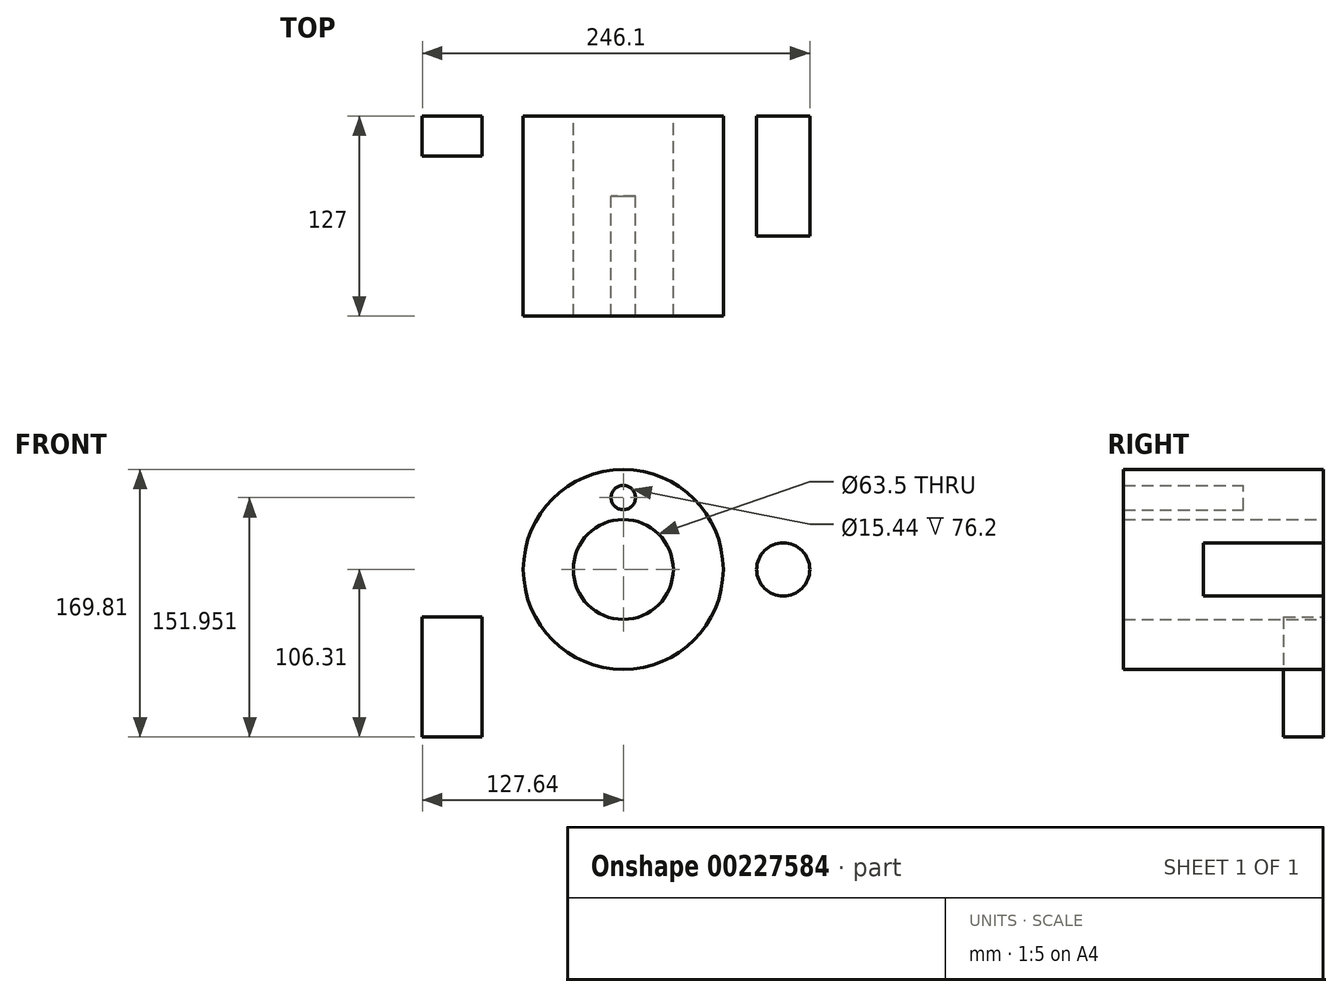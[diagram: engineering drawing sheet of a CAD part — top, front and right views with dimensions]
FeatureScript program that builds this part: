
annotation { "Feature Type Name" : "Feature", "Feature Type Description" : "" }
export const myFeature = defineFeature(function(context is Context, id is Id, definition is map)
    precondition{}
    {
        {
            var Q0;
            Q0=qCreatedBy(makeId("Front.planeOp"),FACE);
            var sketch = newSketch(context, id + "F0", { "sketchPlane" : qUnion([Q0])});
            skCircle(sketch, "E0", {"center": v(0, 0) * mm, "radius": 63.5 * mm});
            skCircle(sketch, "E1", {"center": v(0, 0) * mm, "radius": 31.75 * mm});
            skSolve(sketch);
        }
        {
            var Q0;
            Q0=makeQuery(id+"F0.imprint","IMPRINT",FACE,{"disambiguationData":[TD([[makeQuery(id+"F0.imprint","IMPRINT",EDGE,{"derivedFrom":sQuery(id+"F0.wireOp",EDGE,"E0")}),1.0]])]});
            var Q1;
            Q1 = qSketchRegion(id + "F0", true);
            extrude(context, id + "F1", {"entities" : qUnion([Q0, Q1]), "depth" : 50.8 * mm});
        }
        {
            var Q0;
            Q0=makeQuery(id+"F1.opExtrude","CAP_FACE",FACE,{"disambiguationData":[OSD([sQuery(id+"F0.wireOp",EDGE,"E0"),sQuery(id+"F0.wireOp",EDGE,"E1")])],"isStart":false});
            var sketch = newSketch(context, id + "F2", { "sketchPlane" : qUnion([Q0])});
            skCircle(sketch, "E2", {"center": v(0, 45.64) * mm, "radius": 7.72 * mm});
            skSolve(sketch);
        }
        {
            var Q0;
            Q0 = qSketchRegion(id + "F2", true);
            extrude(context, id + "F3", {"entities" : qUnion([Q0]), "operationType" : NewBodyOperationType.ADD, "oppositeDirection" : true, "depth" : 50.8 * mm});
        }
        {
            var Q0;
            Q0=makeQuery(id+"F2.imprint","IMPRINT",FACE,{"disambiguationData":[TD([[makeQuery(id+"F2.imprint","IMPRINT",EDGE,{"derivedFrom":sQuery(id+"F2.wireOp",EDGE,"E2")}),-1.0]])]});
            var sketch = newSketch(context, id + "F4", { "sketchPlane" : qUnion([Q0])});
            skCircle(sketch, "E3", {"center": v(101.6, 0) * mm, "radius": 16.86 * mm});
            skLineSegment(sketch, "E4", {"start": v(38.29, -51.7) * mm, "end": v(109.34, -14.98) * mm});
            skLineSegment(sketch, "E5", {"start": v(36.14, 52.8) * mm, "end": v(109.34, 14.98) * mm});
            skSolve(sketch);
        }
        {
            var Q0;
            Q0 = qSketchRegion(id + "F4", true);
            extrude(context, id + "F5", {"entities" : qUnion([Q0]), "depth" : 25.4 * mm});
        }
        {
            var Q0;
            Q0=makeQuery(id+"F5.opExtrude","CAP_FACE",FACE,{"disambiguationData":[OSD([sQuery(id+"F4.wireOp",EDGE,"E3")])],"isStart":false});
            extrude(context, id + "F6", {"entities" : qUnion([Q0]), "operationType" : NewBodyOperationType.ADD, "oppositeDirection" : true, "depth" : 76.2 * mm});
        }
        {
            var Q0;
            Q0=makeQuery(id+"F5.opExtrude","CAP_FACE",FACE,{"disambiguationData":[OSD([sQuery(id+"F4.wireOp",EDGE,"E3")])],"isStart":false});
            extrude(context, id + "F7", {"entities" : qUnion([Q0]), "operationType" : NewBodyOperationType.ADD, "oppositeDirection" : true, "depth" : 25.4 * mm});
        }
        {
            var Q0;
            Q0=makeQuery(id+"F2.imprint","IMPRINT",FACE,{"disambiguationData":[TD([[makeQuery(id+"F2.imprint","IMPRINT",EDGE,{"derivedFrom":sQuery(id+"F2.wireOp",EDGE,"E2")}),-1.0]])]});
            extrude(context, id + "F8", {"entities" : qUnion([Q0]), "operationType" : NewBodyOperationType.ADD, "depth" : 76.2 * mm});
        }
        {
            var Q0;
            Q0=qCreatedBy(makeId("Front.planeOp"),FACE);
            var sketch = newSketch(context, id + "F9", { "sketchPlane" : qUnion([Q0])});
            skLineSegment(sketch, "E6.bottom", {"start": v(-127.64, -30.11) * mm, "end": v(-89.54, -30.11) * mm});
            skLineSegment(sketch, "E6.top", {"start": v(-127.64, -106.31) * mm, "end": v(-89.54, -106.31) * mm});
            skLineSegment(sketch, "E6.left", {"start": v(-127.64, -30.11) * mm, "end": v(-127.64, -106.31) * mm});
            skLineSegment(sketch, "E6.right", {"start": v(-89.54, -30.11) * mm, "end": v(-89.54, -106.31) * mm});
            skSolve(sketch);
        }
        {
            var Q0;
            Q0=makeQuery(id+"F9.imprint","IMPRINT",FACE,{"disambiguationData":[TD([[makeQuery(id+"F9.imprint","IMPRINT",EDGE,{"derivedFrom":sQuery(id+"F9.wireOp",EDGE,"E6.bottom")}),-1.0]])]});
            extrude(context, id + "F10", {"entities" : qUnion([Q0]), "depth" : 25.4 * mm});
        }
    });
